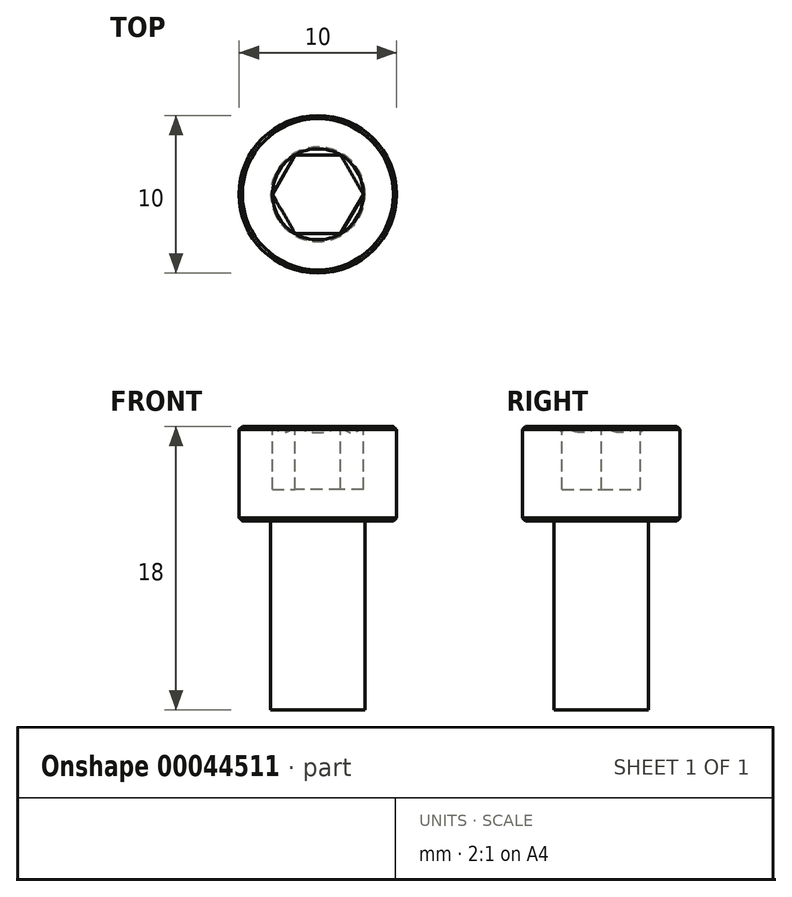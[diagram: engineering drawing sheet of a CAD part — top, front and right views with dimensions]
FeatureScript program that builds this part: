
annotation { "Feature Type Name" : "Feature", "Feature Type Description" : "" }
export const myFeature = defineFeature(function(context is Context, id is Id, definition is map)
    precondition{}
    {
        {
            var Q0;
            Q0=qCreatedBy(makeId("Front.planeOp"),FACE);
            var sketch = newSketch(context, id + "F0", { "sketchPlane" : qUnion([Q0])});
            skLineSegment(sketch, "E0", {"start": v(0, 17.39) * mm, "end": v(0, -18.17) * mm, "construction": true});
            skLineSegment(sketch, "E1", {"start": v(0, 6) * mm, "end": v(5, 6) * mm});
            skLineSegment(sketch, "E2", {"start": v(5, 6) * mm, "end": v(5, 0) * mm});
            skLineSegment(sketch, "E3", {"start": v(5, 0) * mm, "end": v(3, 0) * mm});
            skLineSegment(sketch, "E4", {"start": v(3, 0) * mm, "end": v(3, -12) * mm});
            skLineSegment(sketch, "E5", {"start": v(3, -12) * mm, "end": v(0, -12) * mm});
            skLineSegment(sketch, "E6", {"start": v(0, -12) * mm, "end": v(0, 6) * mm});
            skSolve(sketch);
        }
        {
            var Q0;
            Q0=qSketchRegion(id+"F0",true);
            var Q1;
            Q1=sQuery(id+"F0.wireOp",EDGE,"E0");
            revolve(context, id + "F1", {"entities" : qUnion([Q0]), "axis" : qUnion([Q1]), "revolveType" : RevolveType.FULL});
        }
        {
            var Q0;
            Q0=makeQuery(id+"F1.opRevolve","SWEPT_FACE",FACE,{"disambiguationData":[OSD([sQuery(id+"F0.wireOp",EDGE,"E1")])]});
            var sketch = newSketch(context, id + "F2", { "sketchPlane" : qUnion([Q0])});
            skCircle(sketch, "E7.cCircle", {"center": v(0, 0) * mm, "radius": 2.5 * mm, "construction": true});
            skLineSegment(sketch, "E7.0", {"start": v(-2.89, 0) * mm, "end": v(-1.44, 2.5) * mm});
            skLineSegment(sketch, "E7.1", {"start": v(-1.44, 2.5) * mm, "end": v(1.44, 2.5) * mm});
            skLineSegment(sketch, "E7.2", {"start": v(1.44, 2.5) * mm, "end": v(2.89, 0) * mm});
            skLineSegment(sketch, "E7.3", {"start": v(2.89, 0) * mm, "end": v(1.44, -2.5) * mm});
            skLineSegment(sketch, "E7.4", {"start": v(1.44, -2.5) * mm, "end": v(-1.44, -2.5) * mm});
            skLineSegment(sketch, "E7.5", {"start": v(-1.44, -2.5) * mm, "end": v(-2.89, 0) * mm});
            skPoint(sketch, "E7.0.midPoint", {"position": v(-2.17, 1.25) * mm});
            skSolve(sketch);
        }
        {
            var Q0;
            Q0=qSketchRegion(id+"F2",true);
            extrude(context, id + "F3", {"entities" : qUnion([Q0]), "operationType" : NewBodyOperationType.REMOVE, "oppositeDirection" : true, "depth" : 4 * mm});
        }
        {
            var Q0;
            Q0=qCreatedBy(makeId("Front.planeOp"),FACE);
            var sketch = newSketch(context, id + "F4", { "sketchPlane" : qUnion([Q0])});
            skLineSegment(sketch, "E8", {"start": v(2.5, 5.61) * mm, "end": v(2.89, 6) * mm});
            skLineSegment(sketch, "E9", {"start": v(2.5, 5.61) * mm, "end": v(2.5, 6) * mm});
            skLineSegment(sketch, "E10", {"start": v(2.5, 6) * mm, "end": v(2.89, 6) * mm});
            skLineSegment(sketch, "E11", {"start": v(0, 8.76) * mm, "end": v(0, 3.18) * mm, "construction": true});
            skSolve(sketch);
        }
        {
            var Q0;
            Q0=qSketchRegion(id+"F4",true);
            var Q1;
            Q1=sQuery(id+"F4.wireOp",EDGE,"E11");
            revolve(context, id + "F5", {"operationType" : NewBodyOperationType.REMOVE, "entities" : qUnion([Q0]), "axis" : qUnion([Q1]), "revolveType" : RevolveType.FULL, "oppositeDirection" : true});
        }
        {
            var Q0;
            Q0=makeQuery(id+"F1.opRevolve","SWEPT_EDGE",EDGE,{"disambiguationData":[OSD([sQuery(id+"F0.wireOp",EDGE,"E1"),sQuery(id+"F0.wireOp",EDGE,"E2")])]});
            var Q1;
            Q1=makeQuery(id+"F1.opRevolve","SWEPT_EDGE",EDGE,{"disambiguationData":[OSD([sQuery(id+"F0.wireOp",EDGE,"E2"),sQuery(id+"F0.wireOp",EDGE,"E3")])]});
            chamfer(context, id + "F6", {"entities" : qUnion([Q0, Q1]), "width" : .2 * mm, "tangentPropagation" : true});
        }
    });
